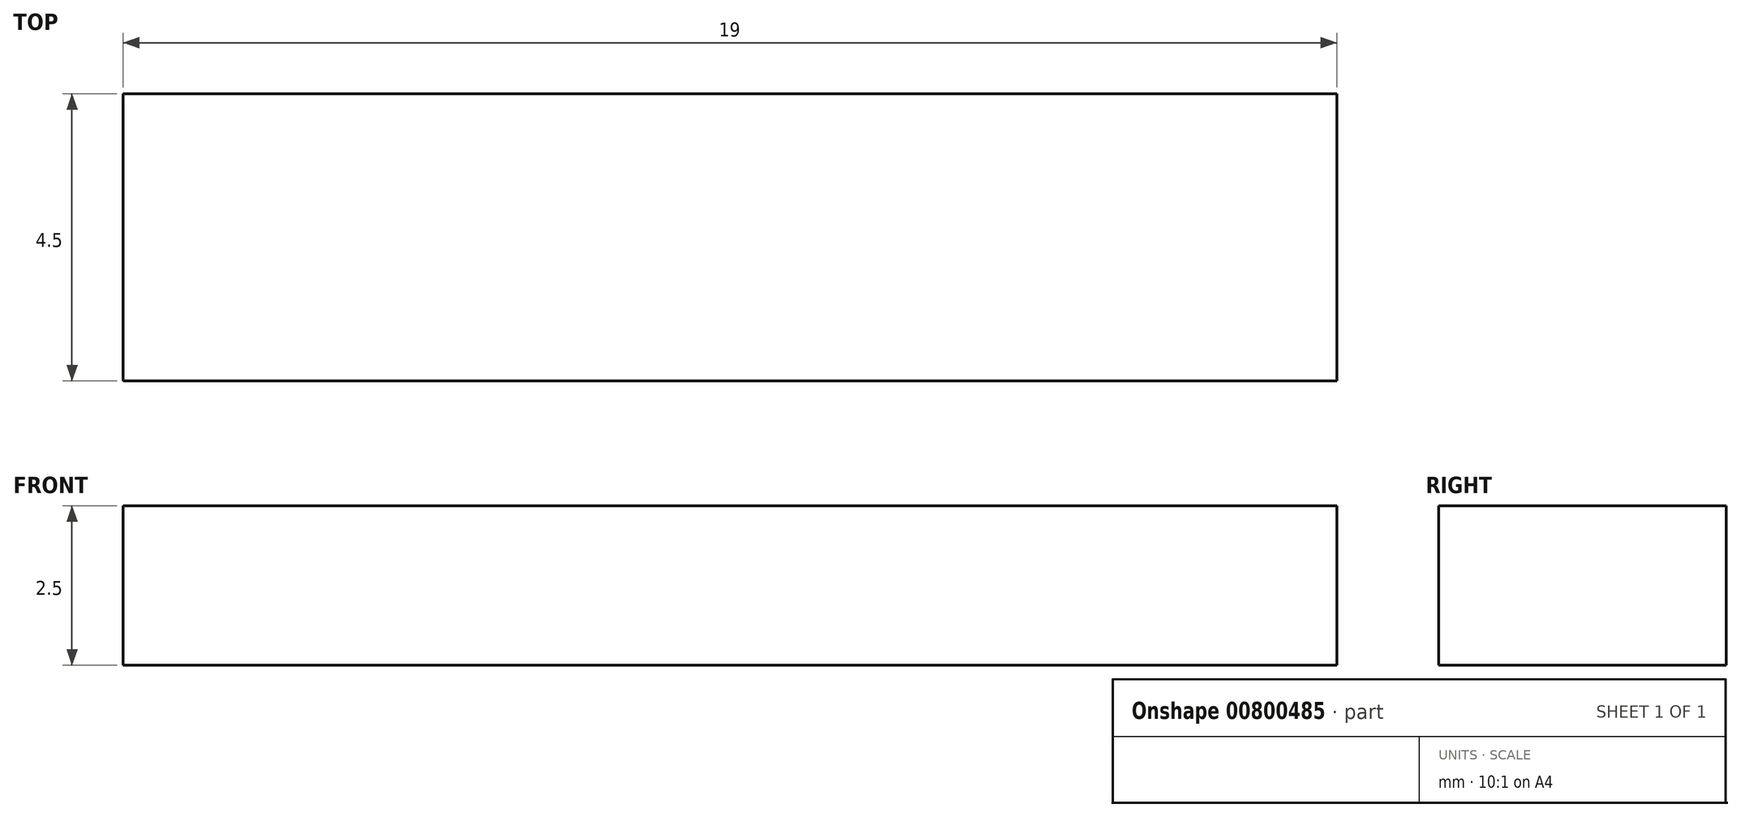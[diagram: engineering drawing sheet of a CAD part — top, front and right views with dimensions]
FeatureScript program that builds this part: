
annotation { "Feature Type Name" : "Feature", "Feature Type Description" : "" }
export const myFeature = defineFeature(function(context is Context, id is Id, definition is map)
    precondition{}
    {
        {
            var Q0;
            Q0=qCreatedBy(makeId("Front.planeOp"),FACE);
            var sketch = newSketch(context, id + "F0", { "sketchPlane" : qUnion([Q0])});
            skLineSegment(sketch, "E0.bottom", {"start": v(-9.5, 1.25) * mm, "end": v(9.5, 1.25) * mm});
            skLineSegment(sketch, "E0.top", {"start": v(-9.5, -1.25) * mm, "end": v(9.5, -1.25) * mm});
            skLineSegment(sketch, "E0.left", {"start": v(-9.5, 1.25) * mm, "end": v(-9.5, -1.25) * mm});
            skLineSegment(sketch, "E0.right", {"start": v(9.5, 1.25) * mm, "end": v(9.5, -1.25) * mm});
            skPoint(sketch, "E0.middle", {"position": v(0, 0) * mm});
            skSolve(sketch);
        }
        {
            var Q0;
            Q0=makeQuery(id+"F0.imprint","IMPRINT",FACE,{"disambiguationData":[TD([[makeQuery(id+"F0.imprint","IMPRINT",EDGE,{"derivedFrom":sQuery(id+"F0.wireOp",EDGE,"E0.bottom")}),-1.0]])]});
            extrude(context, id + "F1", {"entities" : qUnion([Q0]), "depth" : 4.5 * mm, "offsetDistance" : 25 * mm});
        }
    });
